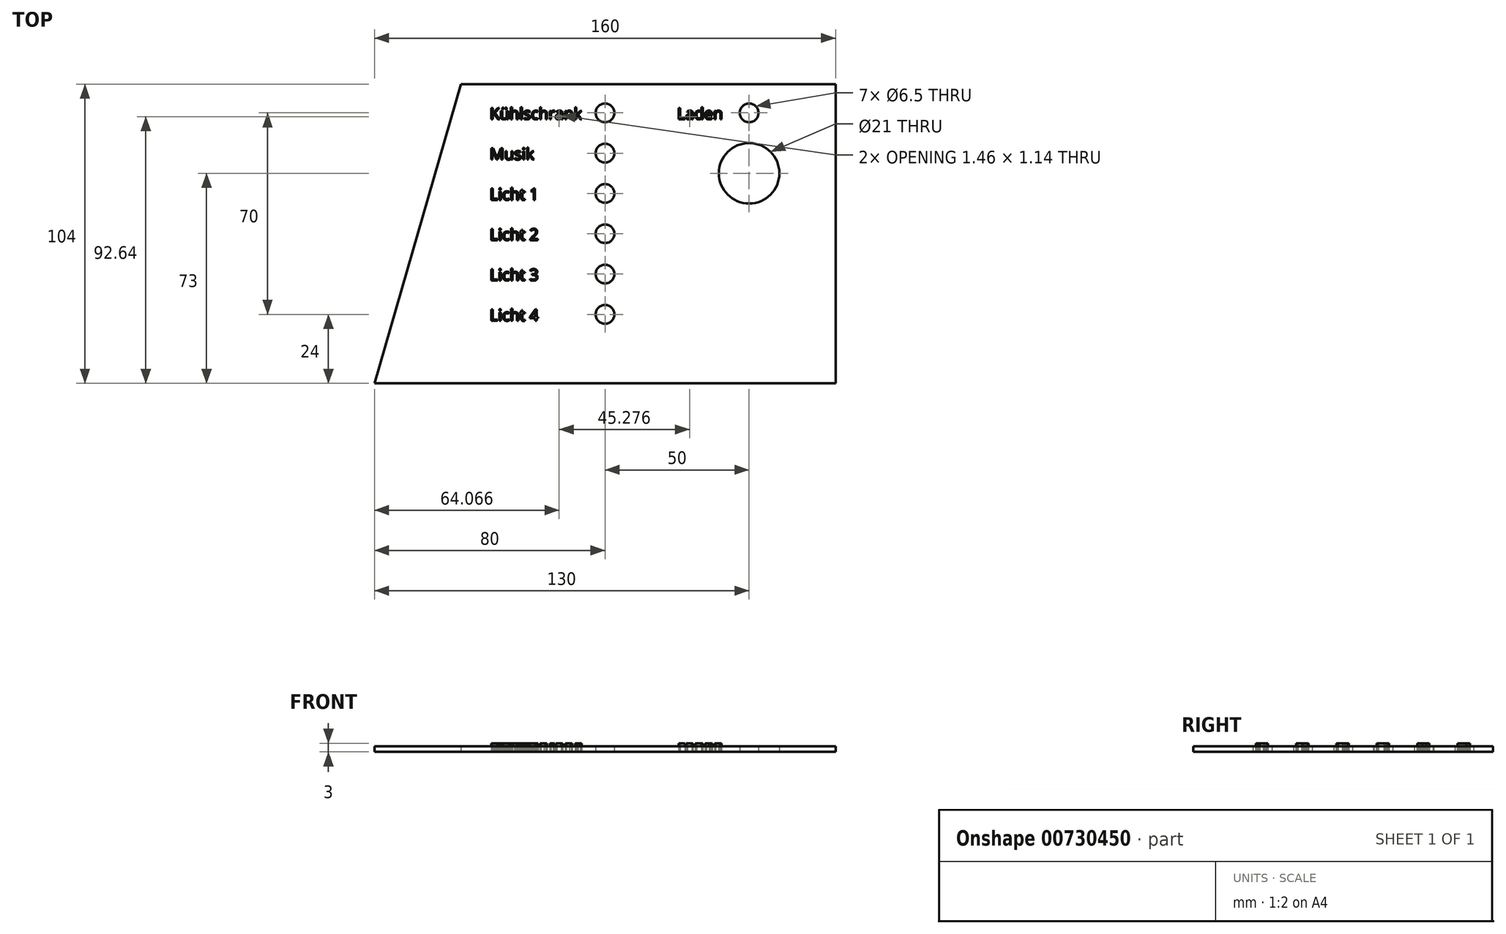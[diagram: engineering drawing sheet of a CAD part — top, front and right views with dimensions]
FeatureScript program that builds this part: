
annotation { "Feature Type Name" : "Feature", "Feature Type Description" : "" }
export const myFeature = defineFeature(function(context is Context, id is Id, definition is map)
    precondition{}
    {
        {
            var Q0;
            Q0=qCreatedBy(makeId("Top.planeOp"),FACE);
            var sketch = newSketch(context, id + "F0", { "sketchPlane" : qUnion([Q0])});
            skLineSegment(sketch, "E0", {"start": v(0, 0) * mm, "end": v(30, 104) * mm});
            skLineSegment(sketch, "E1", {"start": v(30, 104) * mm, "end": v(160, 104) * mm});
            skLineSegment(sketch, "E2", {"start": v(160, 104) * mm, "end": v(160, 0) * mm});
            skLineSegment(sketch, "E3", {"start": v(160, 0) * mm, "end": v(0, 0) * mm});
            skCircle(sketch, "E4", {"center": v(80, 94) * mm, "radius": 3.25 * mm});
            skCircle(sketch, "E5.0.1.0", {"center": v(80, 80) * mm, "radius": 3.25 * mm});
            skCircle(sketch, "E5.0.2.0", {"center": v(80, 66) * mm, "radius": 3.25 * mm});
            skCircle(sketch, "E5.0.3.0", {"center": v(80, 52) * mm, "radius": 3.25 * mm});
            skCircle(sketch, "E5.0.4.0", {"center": v(80, 38) * mm, "radius": 3.25 * mm});
            skCircle(sketch, "E5.0.5.0", {"center": v(80, 24) * mm, "radius": 3.25 * mm});
            skLineSegment(sketch, "E5.direction1", {"start": v(80, 94) * mm, "end": v(151, 94) * mm, "construction": true});
            skLineSegment(sketch, "E5.direction2", {"start": v(80, 94) * mm, "end": v(80, 80) * mm, "construction": true});
            skCircle(sketch, "E6", {"center": v(130, 94) * mm, "radius": 3.25 * mm});
            skCircle(sketch, "E7", {"center": v(130, 73) * mm, "radius": 10.5 * mm});
            skSolve(sketch);
        }
        {
            var Q0;
            Q0=makeQuery(id+"F0.imprint","IMPRINT",FACE,{"disambiguationData":[TD([[makeQuery(id+"F0.imprint","IMPRINT",EDGE,{"derivedFrom":sQuery(id+"F0.wireOp",EDGE,"E0")}),-1.0]])]});
            extrude(context, id + "F1", {"entities" : qUnion([Q0]), "depth" : 2 * mm, "offsetDistance" : 25 * mm});
        }
        {
            var Q0;
            Q0=qCreatedBy(makeId("Top.planeOp"),FACE);
            var sketch = newSketch(context, id + "F2", { "sketchPlane" : qUnion([Q0])});
            skText(sketch, "E8", { "text": "Kühlschrank", "fontName": "OpenSans-Regular.ttf"});
            skText(sketch, "E9", { "text": "Musik", "fontName": "OpenSans-Regular.ttf"});
            skText(sketch, "E10", { "text": "Licht 1", "fontName": "OpenSans-Regular.ttf"});
            skText(sketch, "E11", { "text": "Licht 2", "fontName": "OpenSans-Regular.ttf"});
            skText(sketch, "E12", { "text": "Licht 3", "fontName": "OpenSans-Regular.ttf"});
            skText(sketch, "E13", { "text": "Licht 4", "fontName": "OpenSans-Regular.ttf"});
            skText(sketch, "E14", { "text": "Laden", "fontName": "OpenSans-Regular.ttf"});
            const initialGuessF2  = {"E8": [0.04, 0.09175, 1, 0, 0.004], "E9": [0.04, 0.07775, 1, 0, 0.004], "E10": [0.04, 0.06375, 1, 0, 0.004], "E11": [0.04, 0.04975, 1, 0, 0.004], "E12": [0.04, 0.03575, 1, 0, 0.004], "E13": [0.04, 0.02175, 1, 0, 0.004], "E14": [0.105, 0.09175, 1, 0, 0.004]};
            skSetInitialGuess(sketch, initialGuessF2);
            skSolve(sketch);
        }
        {
            var Q0;
            Q0 = qSketchRegion(id + "F2", true);
            extrude(context, id + "F3", {"entities" : qUnion([Q0]), "depth" : 3 * mm, "offsetDistance" : 25 * mm});
        }
    });
